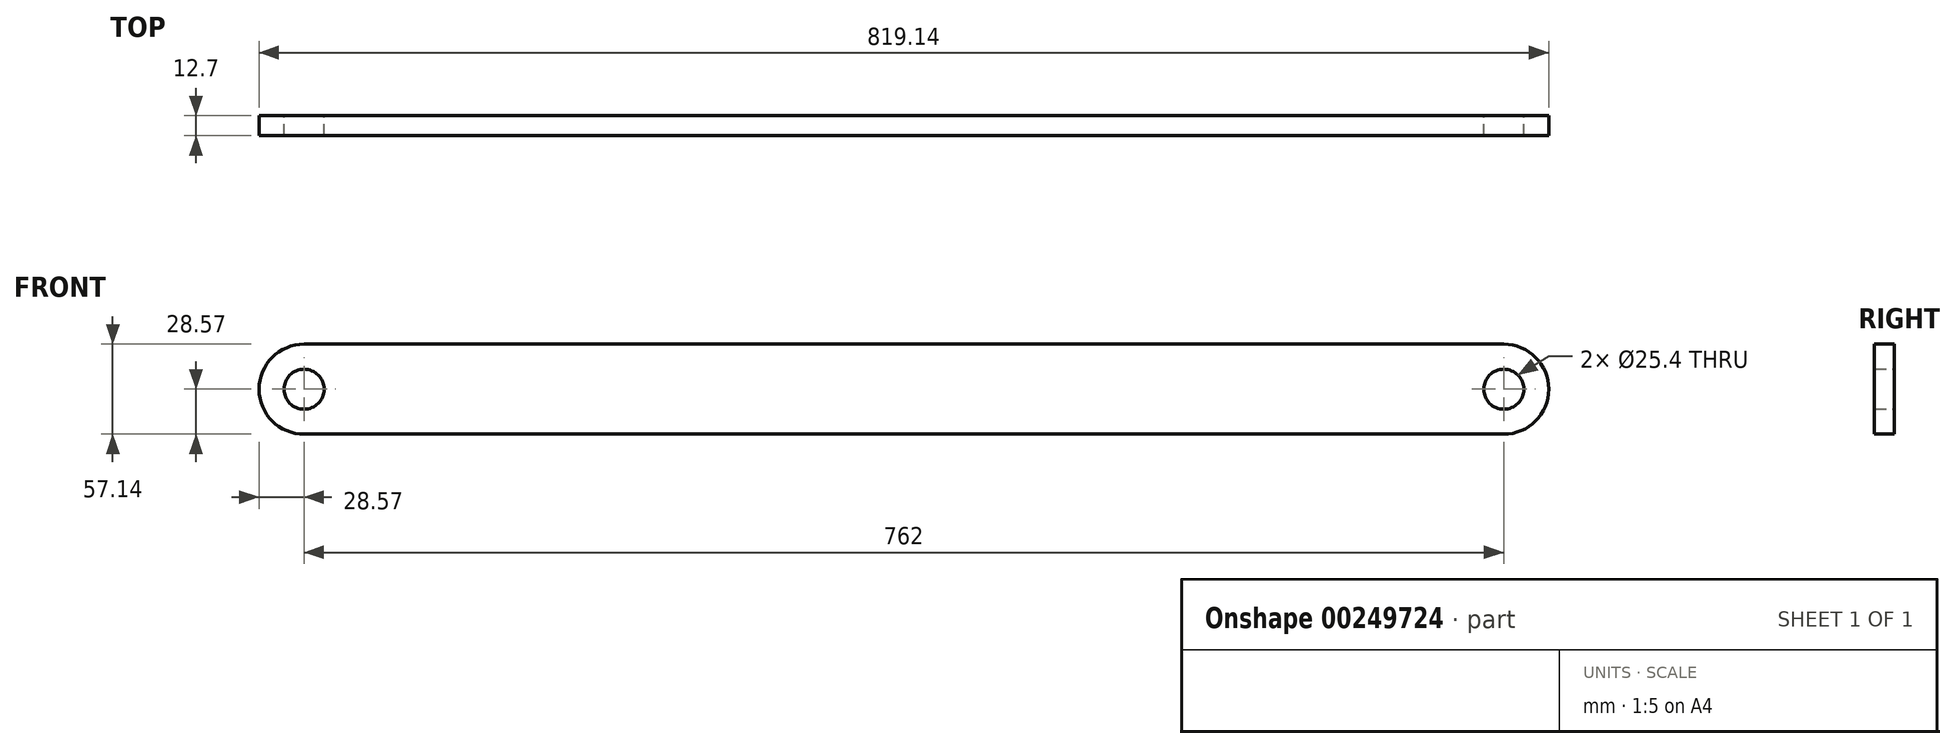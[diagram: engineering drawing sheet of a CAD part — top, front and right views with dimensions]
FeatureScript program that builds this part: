
annotation { "Feature Type Name" : "Feature", "Feature Type Description" : "" }
export const myFeature = defineFeature(function(context is Context, id is Id, definition is map)
    precondition{}
    {
        {
            var Q0;
            Q0=qCreatedBy(makeId("Front.planeOp"),FACE);
            var sketch = newSketch(context, id + "F0", { "sketchPlane" : qUnion([Q0])});
            skLineSegment(sketch, "E0.bottom", {"start": v(381, -28.58) * mm, "end": v(-381, -28.58) * mm});
            skLineSegment(sketch, "E0.top", {"start": v(381, 28.58) * mm, "end": v(-381, 28.58) * mm});
            skLineSegment(sketch, "E0.left", {"start": v(381, -28.58) * mm, "end": v(381, 28.57) * mm});
            skLineSegment(sketch, "E0.right", {"start": v(-381, -28.58) * mm, "end": v(-381, 28.57) * mm});
            skPoint(sketch, "E0.middle", {"position": v(0, 0) * mm});
            skCircle(sketch, "E1", {"center": v(381, 0) * mm, "radius": 28.58 * mm});
            skCircle(sketch, "E2", {"center": v(381, 0) * mm, "radius": 12.7 * mm});
            skCircle(sketch, "E3", {"center": v(-381, 0) * mm, "radius": 28.58 * mm});
            skCircle(sketch, "E4", {"center": v(-381, 0) * mm, "radius": 12.7 * mm});
            skSolve(sketch);
        }
        {
            var Q0;
            Q0 = qSketchRegion(id + "F0", true);
            extrude(context, id + "F1", {"entities" : qUnion([Q0]), "depth" : 12.7 * mm});
        }
    });
